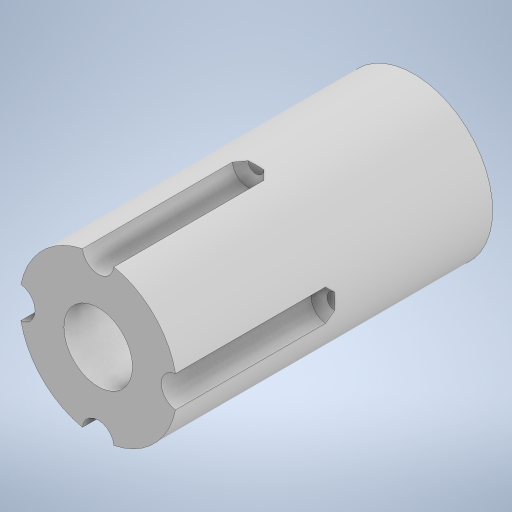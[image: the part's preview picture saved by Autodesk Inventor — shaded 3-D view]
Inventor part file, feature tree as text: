
AUTODESK INVENTOR PART (.ipt)
format: ipt  version: 2023.2 (Build 272271000, 271)  size: 297,472 bytes
history: native  units: mm
features: extrude x4, sketch x4, chamfer x1
ambient origin geometry x8: Origin, YZ Plane, XZ Plane, XY Plane, X Axis, Y Axis, Z Axis, Center Point
bodies: Volumenkörper1 (feature_tree)
feature tree (9):
  extrude  "Extrusion1"  Depth=20.0mm TaperAngle=0.0deg
  extrude  "Extrusion2"  Depth=10.0mm
  extrude  "Extrusion3"  Depth=2.0mm TaperAngle=0.0deg
  extrude  "Extrusion4"  Depth=10.0mm
  chamfer  "Fase6"  Distance=40.0mm Angle=360.0deg
  sketch  "Skizze1"  dims[d0=5.35mm d1=20.0mm d2=0.0mm]
  sketch  "Skizze2"  dims[d3=10.0mm d4=1.0mm]
  sketch  "Skizze3"  dims[d5=40.0mm d7=360.0deg d9=2.0mm d10=0.0mm]
  sketch  "Skizze4"  dims[d11=4.0mm d12=0.0mm d28=2.0mm d29=40.0mm d31=360.0deg d33=10.0mm d34=0.0mm d35=0.5mm d36=2.0mm d37=45.0deg d38=0.872665mm]
